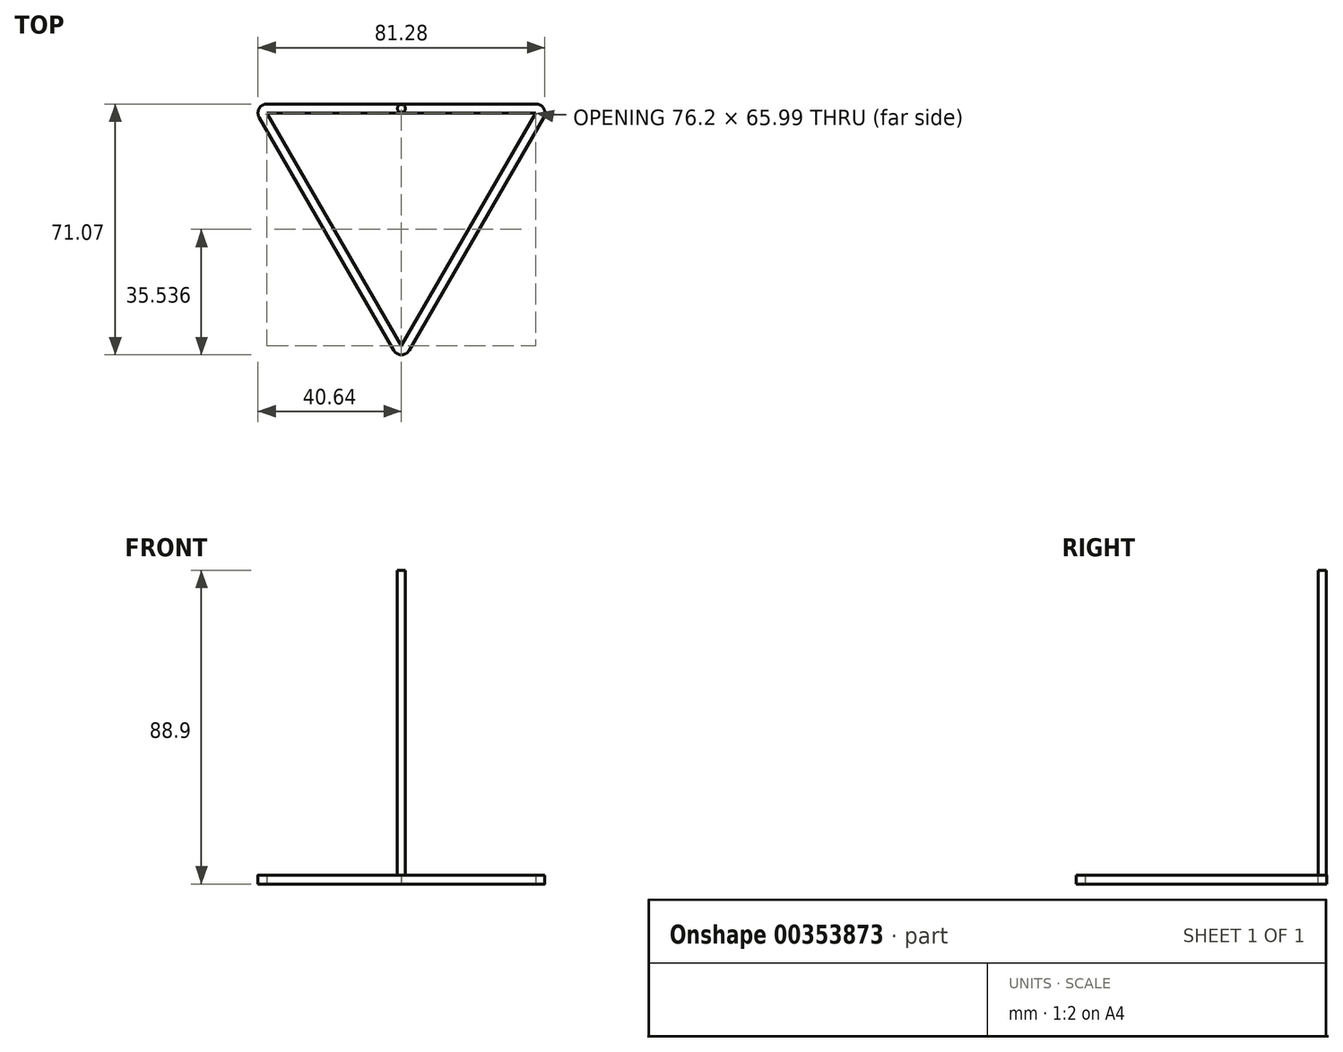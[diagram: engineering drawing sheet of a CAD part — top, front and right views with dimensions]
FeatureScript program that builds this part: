
annotation { "Feature Type Name" : "Feature", "Feature Type Description" : "" }
export const myFeature = defineFeature(function(context is Context, id is Id, definition is map)
    precondition{}
    {
        {
            var Q0;
            Q0=qCreatedBy(makeId("Top.planeOp"),FACE);
            var sketch = newSketch(context, id + "F0", { "sketchPlane" : qUnion([Q0])});
            skLineSegment(sketch, "E0", {"start": v(0, 0) * mm, "end": v(-38.1, 66) * mm});
            skLineSegment(sketch, "E1", {"start": v(-38.1, 66) * mm, "end": v(38.1, 66) * mm});
            skLineSegment(sketch, "E2", {"start": v(38.1, 66) * mm, "end": v(0, 0) * mm});
            skLineSegment(sketch, "E3", {"start": v(-38.1, 68.53) * mm, "end": v(38.1, 68.53) * mm});
            skLineSegment(sketch, "E4", {"start": v(40.3, 64.72) * mm, "end": v(2.2, -1.27) * mm});
            skLineSegment(sketch, "E5", {"start": v(-2.2, -1.27) * mm, "end": v(-40.3, 64.72) * mm});
            skPoint(sketch, "E6.visualSharp", {"position": v(0, -5.08) * mm});
            skArc(sketch, "E6.filletArc", {"start": v(-2.2, -1.27) * mm, "mid": v(0, -2.54) * mm, "end": v(2.2, -1.27) * mm});
            skPoint(sketch, "E7.visualSharp", {"position": v(42.5, 68.53) * mm});
            skArc(sketch, "E7.filletArc", {"start": v(40.3, 64.72) * mm, "mid": v(40.3, 67.26) * mm, "end": v(38.1, 68.53) * mm});
            skPoint(sketch, "E8.visualSharp", {"position": v(-42.5, 68.53) * mm});
            skArc(sketch, "E8.filletArc", {"start": v(-38.1, 68.53) * mm, "mid": v(-40.3, 67.26) * mm, "end": v(-40.3, 64.72) * mm});
            skSolve(sketch);
        }
        {
            var Q0;
            Q0=makeQuery(id+"F0.imprint","IMPRINT",FACE,{"disambiguationData":[TD([[makeQuery(id+"F0.imprint","IMPRINT",EDGE,{"derivedFrom":sQuery(id+"F0.wireOp",EDGE,"E0")}),1.0]])]});
            extrude(context, id + "F1", {"entities" : qUnion([Q0]), "depth" : 2.54 * mm});
        }
        {
            var Q0;
            Q0=qCreatedBy(makeId("Top.planeOp"),FACE);
            var sketch = newSketch(context, id + "F2", { "sketchPlane" : qUnion([Q0])});
            skCircle(sketch, "E9", {"center": v(0, 67.26) * mm, "radius": 1.14 * mm});
            skSolve(sketch);
        }
        {
            var Q0;
            Q0 = qSketchRegion(id + "F2", true);
            extrude(context, id + "F3", {"entities" : qUnion([Q0]), "operationType" : NewBodyOperationType.ADD, "depth" : 88.9 * mm});
        }
    });
